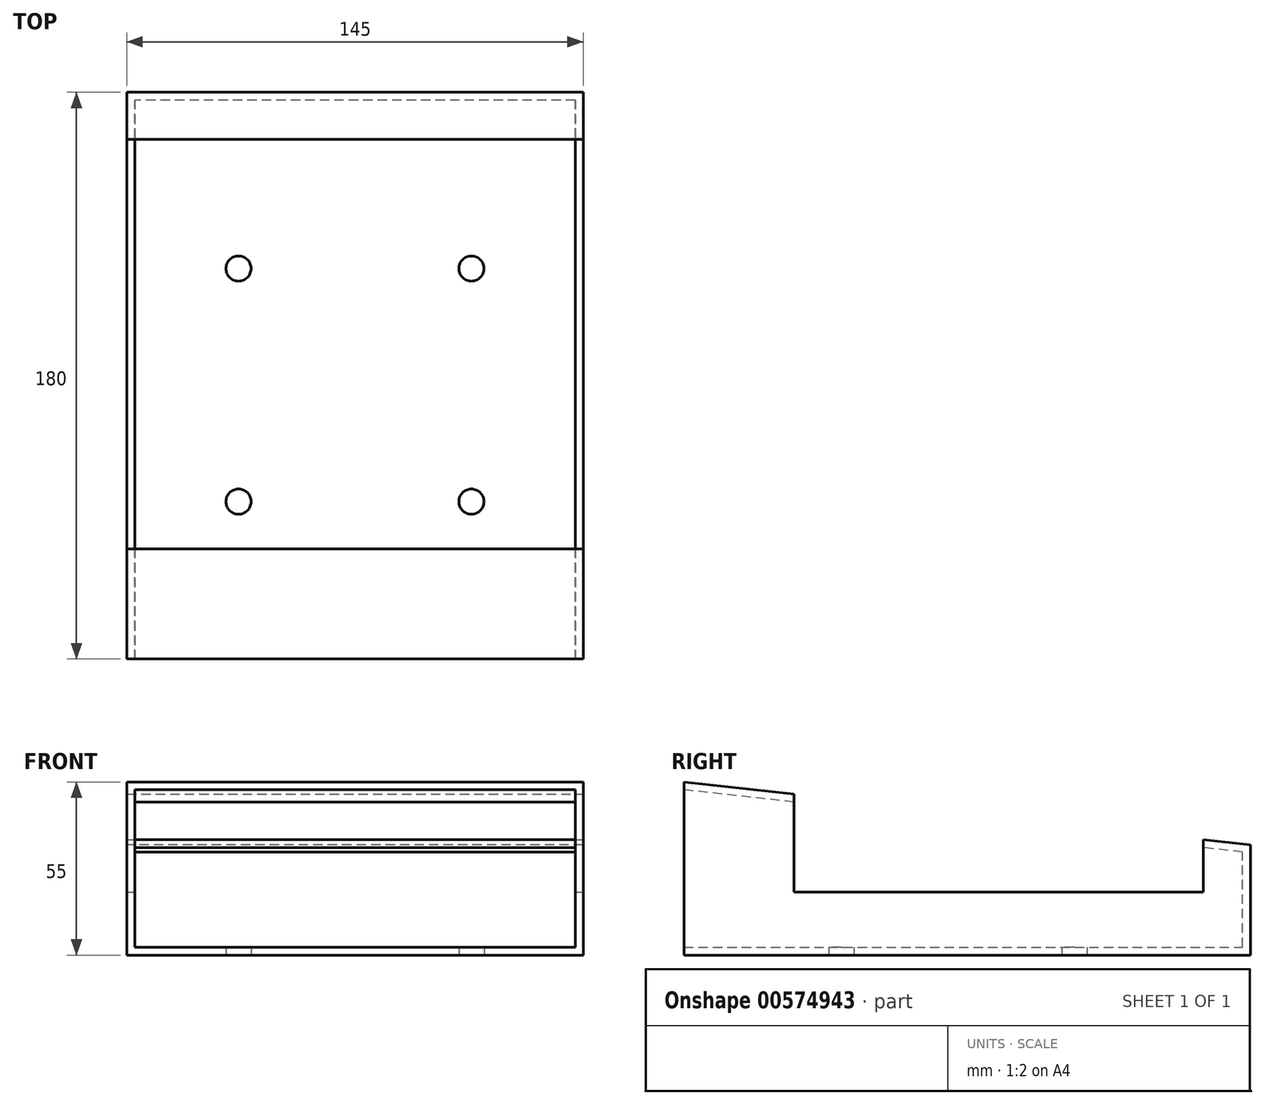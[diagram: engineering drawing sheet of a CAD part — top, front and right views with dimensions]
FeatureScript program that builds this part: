
annotation { "Feature Type Name" : "Feature", "Feature Type Description" : "" }
export const myFeature = defineFeature(function(context is Context, id is Id, definition is map)
    precondition{}
    {
        {
            var Q0;
            Q0=qCreatedBy(makeId("Right.planeOp"),FACE);
            var sketch = newSketch(context, id + "F0", { "sketchPlane" : qUnion([Q0])});
            skLineSegment(sketch, "E0", {"start": v(-70.83, 55) * mm, "end": v(-70.83, 0) * mm});
            skLineSegment(sketch, "E1", {"start": v(-70.83, 0) * mm, "end": v(109.17, 0) * mm});
            skLineSegment(sketch, "E2", {"start": v(109.17, 0) * mm, "end": v(109.17, 35) * mm});
            skLineSegment(sketch, "E3", {"start": v(109.17, 35) * mm, "end": v(-70.83, 55) * mm});
            skSolve(sketch);
        }
        {
            var Q0;
            Q0 = qSketchRegion(id + "F0", true);
            extrude(context, id + "F1", {"entities" : qUnion([Q0]), "depth" : 145 * mm, "offsetDistance" : 25 * mm});
        }
        {
            var Q0;
            Q0=makeQuery(id+"F4xwuvGgOQDok0X_1.boolean.opBoolean","COPY",FACE,{"derivedFrom":makeQuery(id+"F4xwuvGgOQDok0X_1.opExtrude","CAP_FACE",FACE,{"disambiguationData":[OSD([sQuery(id+"FKCM1js2eUwiSbD_1.wireOp",EDGE,"9Rp8IGcE-Iz5m-a7kY-hLu2-NIhZUO8UQLQx"),sQuery(id+"FKCM1js2eUwiSbD_1.wireOp",EDGE,"L0IhzQzI-okNn-15ns-QVHs-RmO0yTnAS5XA"),sQuery(id+"FKCM1js2eUwiSbD_1.wireOp",EDGE,"qdw9iYHc-Bzqu-dEvB-RPXJ-UVlvhCcEYYj0"),sQuery(id+"FKCM1js2eUwiSbD_1.wireOp",EDGE,"zLj74zVD-TuVv-9ju6-SDZv-RvV0RXlGxreU")])],"isStart":false})});
            var Q1;
            Q1=makeQuery(id+"F4xwuvGgOQDok0X_1.boolean.opBoolean","COPY",FACE,{"derivedFrom":makeQuery(id+"F4xwuvGgOQDok0X_1.opExtrude","SWEPT_FACE",FACE,{"disambiguationData":[OSD([sQuery(id+"FKCM1js2eUwiSbD_1.wireOp",EDGE,"9Rp8IGcE-Iz5m-a7kY-hLu2-NIhZUO8UQLQx")])]})});
            var Q2;
            Q2=makeQuery(id+"F1.opExtrude","SWEPT_FACE",FACE,{"disambiguationData":[OSD([sQuery(id+"F0.wireOp",EDGE,"E0")])]});
            shell(context, id + "F2", {"entities" : qUnion([Q0, Q1, Q2]), "thickness" : 2.5 * mm});
        }
        {
            var Q0;
            Q0=makeQuery(id+"F1.opExtrude","CAP_FACE",FACE,{"disambiguationData":[OSD([sQuery(id+"F0.wireOp",EDGE,"E0"),sQuery(id+"F0.wireOp",EDGE,"E1"),sQuery(id+"F0.wireOp",EDGE,"E2"),sQuery(id+"F0.wireOp",EDGE,"E3")])],"isStart":false});
            var sketch = newSketch(context, id + "F3", { "sketchPlane" : qUnion([Q0])});
            skLineSegment(sketch, "E4", {"start": v(-35.83, 51.11) * mm, "end": v(94.17, 36.67) * mm});
            skLineSegment(sketch, "E5", {"start": v(-35.83, 20) * mm, "end": v(94.17, 20) * mm});
            skLineSegment(sketch, "E6", {"start": v(-35.83, 51.11) * mm, "end": v(-35.83, 20) * mm});
            skLineSegment(sketch, "E7", {"start": v(94.17, 20) * mm, "end": v(94.17, 36.67) * mm});
            skSolve(sketch);
        }
        {
            var Q0;
            Q0=makeQuery(id+"F3.imprint","IMPRINT",FACE,{"disambiguationData":[TD([[makeQuery(id+"F3.imprint","IMPRINT",EDGE,{"derivedFrom":sQuery(id+"F3.wireOp",EDGE,"E4")}),1.0]])]});
            extrude(context, id + "F4", {"entities" : qUnion([Q0]), "operationType" : NewBodyOperationType.REMOVE, "oppositeDirection" : true, "depth" : 145 * mm, "offsetDistance" : 25 * mm});
        }
        {
            var Q0;
            Q0=makeQuery(id+"F1.opExtrude","SWEPT_FACE",FACE,{"disambiguationData":[OSD([sQuery(id+"F0.wireOp",EDGE,"E1")])]});
            var sketch = newSketch(context, id + "F5", { "sketchPlane" : qUnion([Q0])});
            skCircle(sketch, "E8", {"center": v(35.5, 20.83) * mm, "radius": 4 * mm});
            skCircle(sketch, "E9", {"center": v(109.5, -53.17) * mm, "radius": 4 * mm});
            skCircle(sketch, "E10", {"center": v(109.5, 20.83) * mm, "radius": 4 * mm});
            skCircle(sketch, "E11", {"center": v(35.5, -53.17) * mm, "radius": 4 * mm});
            skSolve(sketch);
        }
        {
            var Q0;
            Q0=sQuery(id+"F5.wireOp",VERTEX,"E10.center");
            var Q1;
            Q1=sQuery(id+"F5.wireOp",VERTEX,"E8.center");
            var Q2;
            Q2=sQuery(id+"F5.wireOp",VERTEX,"E11.center");
            var Q3;
            Q3=sQuery(id+"F5.wireOp",VERTEX,"E9.center");
            var Q4;
            Q4=makeQuery(id+"F1.opExtrude","SWEPT_BODY",BODY,{"disambiguationData":[OSD([sQuery(id+"F0.wireOp",EDGE,"E0"),sQuery(id+"F0.wireOp",EDGE,"E1"),sQuery(id+"F0.wireOp",EDGE,"E2"),sQuery(id+"F0.wireOp",EDGE,"E3")])]});
            hole(context, id + "F6", {"style" : HoleStyle.SIMPLE, "endStyle" : HoleEndStyle.THROUGH, "holeDiameter" : 8 * mm, "isTappedThrough" : true, "tappedDepth" : 12 * mm, "tapClearance" : 3, "locations" : qUnion([Q0, Q1, Q2, Q3]), "scope" : qUnion([Q4])});
        }
    });
